# Revit family: Haworth_Fern_Chair_Task_Executive
name_source: partatom
category: Furniture
revit_build: Autodesk Revit 2018 (Build: 20170223_1515(x64)
units: mm (PartAtom-declared; Revit-internal decimal feet)

## family parameters
Always vertical = Yes
Cut with Voids When Loaded = No
OmniClass Number = 23.40.20.00
OmniClass Title = General Furniture and Specialties
Room Calculation Point = No
Shared = No
Work Plane-Based = No

## types (8) — shared parameters
Assembly Code = E2020200
Caster Finish = Haworth _ Polymer _ Fog
Depth = 2' - 0"
Description = Haworth Fern Chair Task
Hardware Finish = Haworth _ Polymer _ Black
Height = 3' - 8"
Manufacturer = Haworth
Model = SFx-U0
Post Finish = Haworth _ Metal _ Polished Aluminum
URL = http://www.haworth.com
URL - Product = https://www.haworth.com
Version = 4
Warranty = http://www.haworth.com
Width = 2' - 4"

## per-type parameters (varying)
| type | 4D Arms | Fixed Arms | Height Adjustable Arms | Ht Adj Arms Actual | Low Base | Standard Base | Without Arms |
| SFx-U0-7 - 4D Arms - Standard Base | Yes | No | No | Yes | No | Yes | No |
| SFx-U0-4 - Height Adjustable Arms - Standard Base | No | No | Yes | Yes | No | Yes | No |
| SFx-U0-1 - Fixed Arms - Standard Base | No | Yes | No | No | No | Yes | No |
| SFx-U0-0 - Without Arms - Standard Base | No | No | No | No | No | Yes | Yes |
| SFx-U0-0 - Without Arms - Low Base | No | No | No | No | Yes | No | Yes |
| SFx-U0-1 - Fixed Arms - Low Base | No | Yes | No | No | Yes | No | No |
| SFx-U0-4 - Height Adjustable Arms - Low Base | No | No | Yes | Yes | Yes | No | No |
| SFx-U0-7 - 4D Arms - Low Base | Yes | No | No | Yes | Yes | No | No |

## geometry (parser evidence)
native form markers: Sweep x16
no freeform markers — native parametric forms only
